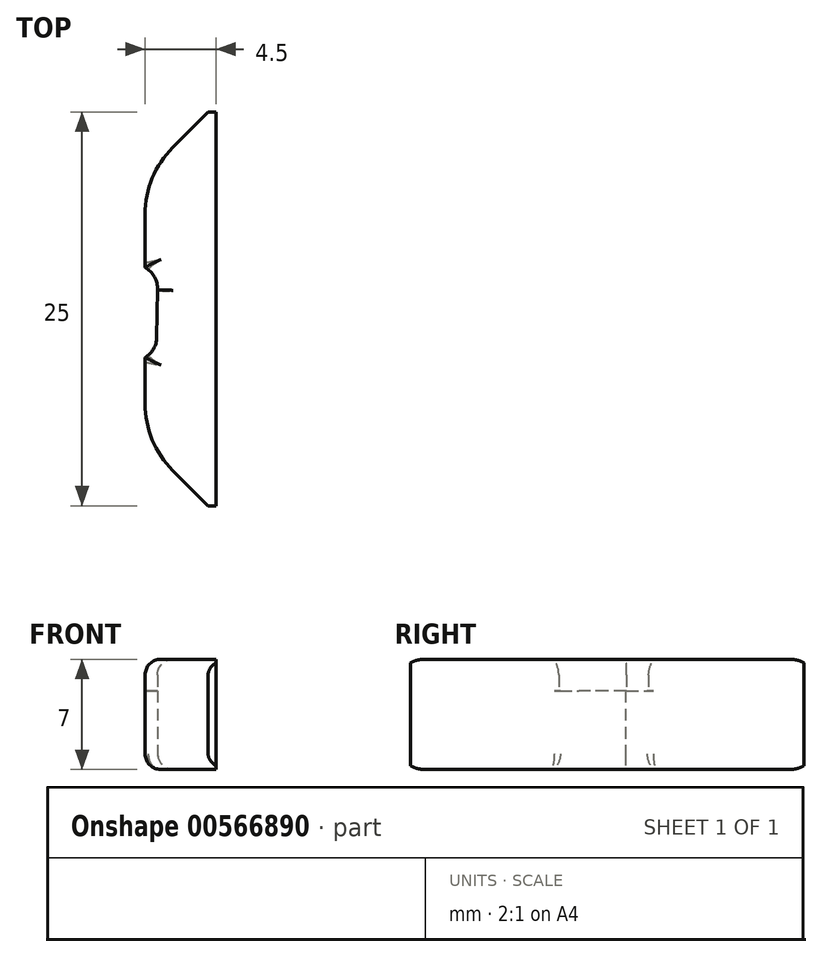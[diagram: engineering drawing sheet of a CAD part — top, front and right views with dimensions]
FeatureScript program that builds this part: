
annotation { "Feature Type Name" : "Feature", "Feature Type Description" : "" }
export const myFeature = defineFeature(function(context is Context, id is Id, definition is map)
    precondition{}
    {
        {
            var Q0;
            Q0=qCreatedBy(makeId("Top.planeOp"),FACE);
            var sketch = newSketch(context, id + "F0", { "sketchPlane" : qUnion([Q0])});
            skLineSegment(sketch, "E0.bottom", {"start": v(2.25, -12.5) * mm, "end": v(-2.25, -12.5) * mm});
            skLineSegment(sketch, "E0.top", {"start": v(2.25, 12.5) * mm, "end": v(-2.25, 12.5) * mm});
            skLineSegment(sketch, "E0.left", {"start": v(2.25, -12.5) * mm, "end": v(2.25, 12.5) * mm});
            skLineSegment(sketch, "E0.right", {"start": v(-2.25, -12.5) * mm, "end": v(-2.25, 12.5) * mm});
            skPoint(sketch, "E0.middle", {"position": v(0, 0) * mm});
            skPoint(sketch, "E1", {"position": v(-2.25, 0) * mm});
            skCircle(sketch, "E2", {"center": v(-2.95, 1.33) * mm, "radius": 1.5 * mm});
            skPoint(sketch, "E2.second.point", {"position": v(-2.25, 2.65) * mm});
            skPoint(sketch, "E2.third.point", {"position": v(-3.94, 2.45) * mm});
            skCircle(sketch, "E3", {"center": v(-2.99, -1.8) * mm, "radius": 1.5 * mm});
            skLineSegment(sketch, "E4", {"start": v(-1.46, 1.46) * mm, "end": v(-1.49, -1.8) * mm});
            skSolve(sketch);
        }
        {
            var Q0;
            Q0=makeQuery(id+"F0.imprint","IMPRINT",FACE,{"disambiguationData":[TD([[makeQuery(id+"F0.imprint","IMPRINT",EDGE,{"derivedFrom":sQuery(id+"F0.wireOp",EDGE,"E0.bottom")}),-1.0]])]});
            var Q1;
            Q1 = qSketchRegion(id + "F2", true);
            extrude(context, id + "F1", {"entities" : qUnion([Q0, Q1]), "depth" : 2 * mm, "offsetDistance" : 25 * mm});
        }
        {
            var Q0;
            Q0=makeQuery(id+"F1.opExtrude","CAP_FACE",FACE,{"disambiguationData":[OSD([sQuery(id+"F0.wireOp",EDGE,"E0.bottom"),sQuery(id+"F0.wireOp",EDGE,"E0.top"),sQuery(id+"F0.wireOp",EDGE,"E0.left"),sQuery(id+"F0.wireOp",EDGE,"E0.right"),sQuery(id+"F0.wireOp",EDGE,"E2"),sQuery(id+"F0.wireOp",EDGE,"E3"),sQuery(id+"F0.wireOp",EDGE,"E4")])],"isStart":false});
            var sketch = newSketch(context, id + "F2", { "sketchPlane" : qUnion([Q0])});
            skLineSegment(sketch, "E5.bottom", {"start": v(-2.25, 12.5) * mm, "end": v(2.25, 12.5) * mm});
            skLineSegment(sketch, "E5.top", {"start": v(-2.25, -12.5) * mm, "end": v(2.25, -12.5) * mm});
            skLineSegment(sketch, "E5.left", {"start": v(-2.25, 12.5) * mm, "end": v(-2.25, 5.3) * mm});
            skLineSegment(sketch, "E5.right", {"start": v(2.25, 12.5) * mm, "end": v(2.25, -12.5) * mm});
            skLineSegment(sketch, "E6.trimOffspring", {"start": v(-2.25, -3.1) * mm, "end": v(-2.25, -4.4) * mm});
            skArc(sketch, "E7", {"start": v(-1.46, 1.15) * mm, "mid": v(-1.62, 2.02) * mm, "end": v(-2.25, 2.65) * mm});
            skLineSegment(sketch, "E8", {"start": v(-1.46, 1.46) * mm, "end": v(-1.46, 1.15) * mm});
            skLineSegment(sketch, "E9", {"start": v(-1.48, -0.94) * mm, "end": v(-1.49, -1.8) * mm});
            skLineSegment(sketch, "E10", {"start": v(-1.49, -1.8) * mm, "end": v(-1.52, -2.12) * mm});
            skArc(sketch, "E11.0", {"start": v(0.03, 0.97) * mm, "mid": v(-0.3, 2.72) * mm, "end": v(-1.55, 3.98) * mm});
            skLineSegment(sketch, "E12.0", {"start": v(0.04, 1.16) * mm, "end": v(0.01, -1.8) * mm});
            skArc(sketch, "E13.0", {"start": v(-1.51, -4.4) * mm, "mid": v(-0.4, -3.3) * mm, "end": v(0.01, -1.8) * mm});
            skLineSegment(sketch, "E14", {"start": v(-1.55, 3.98) * mm, "end": v(-2.25, 3.98) * mm});
            skLineSegment(sketch, "E15", {"start": v(-1.51, -4.4) * mm, "end": v(-2.25, -4.4) * mm});
            skArc(sketch, "E16.0", {"start": v(1.52, 0.8) * mm, "mid": v(1.03, 3.42) * mm, "end": v(-0.85, 5.3) * mm});
            skLineSegment(sketch, "E17.0", {"start": v(1.54, 1.14) * mm, "end": v(1.51, -1.82) * mm});
            skArc(sketch, "E18.0", {"start": v(-0.78, -5.72) * mm, "mid": v(0.9, -4.07) * mm, "end": v(1.51, -1.8) * mm});
            skLineSegment(sketch, "E19", {"start": v(-0.85, 5.3) * mm, "end": v(-2.25, 5.3) * mm});
            skLineSegment(sketch, "E20", {"start": v(-0.78, -5.72) * mm, "end": v(-2.25, -5.72) * mm});
            skLineSegment(sketch, "E21.trimOffspring", {"start": v(-2.25, 3.98) * mm, "end": v(-2.25, 2.65) * mm});
            skLineSegment(sketch, "E22.trimOffspring", {"start": v(-2.25, -5.72) * mm, "end": v(-2.25, -12.5) * mm});
            skSolve(sketch);
        }
        {
            var Q0;
            {var subQ14=sQuery(id+"F2.wireOp",EDGE,"E6.trimOffspring");Q0=makeQuery(id+"F2.imprint","IMPRINT",FACE,{"disambiguationData":[TD([[makeQuery(id+"F2.imprint","IMPRINT",EDGE,{"derivedFrom":subQ14}),-1.0]])]});}
            var Q1;
            Q1=makeQuery(id+"F2.imprint","IMPRINT",FACE,{"disambiguationData":[TD([[makeQuery(id+"F2.imprint","IMPRINT",EDGE,{"derivedFrom":sQuery(id+"F2.wireOp",EDGE,"E5.bottom")}),1.0]])]});
            extrude(context, id + "F3", {"entities" : qUnion([Q0, Q1]), "operationType" : NewBodyOperationType.ADD, "depth" : 3 * mm, "offsetDistance" : 25 * mm});
        }
        {
            var Q0;
            Q0=makeQuery(id+"F3.opExtrude","CAP_FACE",FACE,{"disambiguationData":[OSD([sQuery(id+"F2.wireOp",EDGE,"E5.bottom"),sQuery(id+"F2.wireOp",EDGE,"E5.top"),sQuery(id+"F2.wireOp",EDGE,"E5.left"),sQuery(id+"F2.wireOp",EDGE,"E5.right"),sQuery(id+"F2.wireOp",EDGE,"E16.0"),sQuery(id+"F2.wireOp",EDGE,"E17.0"),sQuery(id+"F2.wireOp",EDGE,"E18.0"),sQuery(id+"F2.wireOp",EDGE,"E19"),sQuery(id+"F2.wireOp",EDGE,"E20"),sQuery(id+"F2.wireOp",EDGE,"E22.trimOffspring")])],"isStart":false});
            var sketch = newSketch(context, id + "F4", { "sketchPlane" : qUnion([Q0])});
            skLineSegment(sketch, "E23.bottom", {"start": v(-2.25, 12.5) * mm, "end": v(2.25, 12.5) * mm});
            skLineSegment(sketch, "E23.top", {"start": v(-2.25, -12.5) * mm, "end": v(2.25, -12.5) * mm});
            skLineSegment(sketch, "E23.left", {"start": v(-2.25, 12.5) * mm, "end": v(-2.25, 2.63) * mm});
            skLineSegment(sketch, "E23.right", {"start": v(2.25, 12.5) * mm, "end": v(2.25, -12.5) * mm});
            skArc(sketch, "E24", {"start": v(-1.47, 1.22) * mm, "mid": v(-1.65, 2.04) * mm, "end": v(-2.25, 2.63) * mm});
            skArc(sketch, "E25", {"start": v(-2.25, -3.08) * mm, "mid": v(-1.71, -2.54) * mm, "end": v(-1.5, -1.81) * mm});
            skLineSegment(sketch, "E26", {"start": v(-1.47, 1.22) * mm, "end": v(-1.5, -1.81) * mm});
            skLineSegment(sketch, "E27.trimOffspring", {"start": v(-2.25, -3.08) * mm, "end": v(-2.25, -12.5) * mm});
            skSolve(sketch);
        }
        {
            var Q0;
            Q0 = qSketchRegion(id + "F4", true);
            extrude(context, id + "F5", {"entities" : qUnion([Q0]), "operationType" : NewBodyOperationType.ADD, "depth" : 2 * mm, "offsetDistance" : 25 * mm});
        }
        {
            var Q0;
            Q0=makeQuery(id+"F3.opExtrude","SWEPT_EDGE",EDGE,{"disambiguationData":[OSD([sQuery(id+"F0.wireOp",EDGE,"E0.right"),sQuery(id+"F2.wireOp",EDGE,"E6.trimOffspring"),sQuery(id+"F2.wireOp",EDGE,"E15")])]});
            var Q1;
            Q1=makeQuery(id+"F3.opExtrude","SWEPT_EDGE",EDGE,{"disambiguationData":[OSD([sQuery(id+"F0.wireOp",EDGE,"E0.right"),sQuery(id+"F2.wireOp",EDGE,"E14"),sQuery(id+"F2.wireOp",EDGE,"E21.trimOffspring")])]});
            fillet(context, id + "F6", {"entities" : qUnion([Q0, Q1]), "radius" : .5 * mm, "tangentPropagation" : true, "allowEdgeOverflow" : false});
        }
        {
            var Q0;
            Q0=makeQuery(id+"F5.boolean.opBoolean","MERGE",EDGE,{"derivedFrom":[makeQuery(id+"F3.boolean.opBoolean","MERGE",EDGE,{"derivedFrom":[makeQuery(id+"F1.opExtrude","SWEPT_EDGE",EDGE,{"disambiguationData":[OSD([sQuery(id+"F0.wireOp",EDGE,"E0.top"),sQuery(id+"F0.wireOp",EDGE,"E0.right")])]}),makeQuery(id+"F3.opExtrude","SWEPT_EDGE",EDGE,{"disambiguationData":[OSD([sQuery(id+"F2.wireOp",EDGE,"E5.bottom"),sQuery(id+"F2.wireOp",EDGE,"E5.left")])]})]}),makeQuery(id+"F5.opExtrude","SWEPT_EDGE",EDGE,{"disambiguationData":[OSD([sQuery(id+"F4.wireOp",EDGE,"E23.bottom"),sQuery(id+"F4.wireOp",EDGE,"E23.left")])]})]});
            var Q1;
            Q1=makeQuery(id+"F5.boolean.opBoolean","MERGE",EDGE,{"derivedFrom":[makeQuery(id+"F3.boolean.opBoolean","MERGE",EDGE,{"derivedFrom":[makeQuery(id+"F1.opExtrude","SWEPT_EDGE",EDGE,{"disambiguationData":[OSD([sQuery(id+"F0.wireOp",EDGE,"E0.bottom"),sQuery(id+"F0.wireOp",EDGE,"E0.right")])]}),makeQuery(id+"F3.opExtrude","SWEPT_EDGE",EDGE,{"disambiguationData":[OSD([sQuery(id+"F2.wireOp",EDGE,"E5.top"),sQuery(id+"F2.wireOp",EDGE,"E22.trimOffspring")])]})]}),makeQuery(id+"F5.opExtrude","SWEPT_EDGE",EDGE,{"disambiguationData":[OSD([sQuery(id+"F4.wireOp",EDGE,"E23.top"),sQuery(id+"F4.wireOp",EDGE,"E27.trimOffspring")])]})]});
            chamfer(context, id + "F7", {"entities" : qUnion([Q0, Q1]), "width" : 4 * mm, "tangentPropagation" : true});
        }
        {
            var Q0;
            {var subQ0=sQuery(id+"F4.wireOp",EDGE,"E23.left");var subQ1=sQuery(id+"F2.wireOp",EDGE,"E5.left");var subQ2=sQuery(id+"F0.wireOp",EDGE,"E0.right");var subQ3=sQuery(id+"F0.wireOp",EDGE,"E0.top");Q0=makeQuery(id+"F7.opChamfer","BLEND_EDGE",EDGE,{"blendedFrom":[makeQuery(id+"F5.boolean.opBoolean","MERGE",EDGE,{"derivedFrom":[makeQuery(id+"F3.boolean.opBoolean","MERGE",EDGE,{"derivedFrom":[makeQuery(id+"F1.opExtrude","SWEPT_EDGE",EDGE,{"disambiguationData":[OSD([subQ3,subQ2])]}),makeQuery(id+"F3.opExtrude","SWEPT_EDGE",EDGE,{"disambiguationData":[OSD([sQuery(id+"F2.wireOp",EDGE,"E5.bottom"),subQ1])]})]}),makeQuery(id+"F5.opExtrude","SWEPT_EDGE",EDGE,{"disambiguationData":[OSD([sQuery(id+"F4.wireOp",EDGE,"E23.bottom"),subQ0])]})]}),makeQuery(id+"F5.boolean.opBoolean","MERGE",FACE,{"derivedFrom":[makeQuery(id+"F3.boolean.opBoolean","MERGE",FACE,{"derivedFrom":[makeQuery(id+"F1.opExtrude","SWEPT_FACE",FACE,{"disambiguationData":[OSD([subQ2]),TDD([makeQuery(id+"F0.imprint","IMPRINT",EDGE,{"disambiguationData":[TD([[makeQuery(id+"F0.imprint","INTERSECT",VERTEX,{"derivedFrom":[subQ3,subQ2]}),1.0]])],"derivedFrom":subQ2})])]}),makeQuery(id+"F3.opExtrude","SWEPT_FACE",FACE,{"disambiguationData":[OSD([subQ1])]}),makeQuery(id+"F3.opExtrude","SWEPT_FACE",FACE,{"disambiguationData":[OSD([sQuery(id+"F2.wireOp",EDGE,"E21.trimOffspring")])]})]}),makeQuery(id+"F5.opExtrude","SWEPT_FACE",FACE,{"disambiguationData":[OSD([subQ0])]})]})],"blendedInto":[makeQuery(id+"F5.boolean.opBoolean","MERGE",FACE,{"derivedFrom":[makeQuery(id+"F3.boolean.opBoolean","MERGE",FACE,{"derivedFrom":[makeQuery(id+"F1.opExtrude","SWEPT_FACE",FACE,{"disambiguationData":[OSD([subQ2]),TDD([makeQuery(id+"F0.imprint","IMPRINT",EDGE,{"disambiguationData":[TD([[makeQuery(id+"F0.imprint","INTERSECT",VERTEX,{"derivedFrom":[subQ3,subQ2]}),1.0]])],"derivedFrom":subQ2})])]}),makeQuery(id+"F3.opExtrude","SWEPT_FACE",FACE,{"disambiguationData":[OSD([subQ1])]}),makeQuery(id+"F3.opExtrude","SWEPT_FACE",FACE,{"disambiguationData":[OSD([sQuery(id+"F2.wireOp",EDGE,"E21.trimOffspring")])]})]}),makeQuery(id+"F5.opExtrude","SWEPT_FACE",FACE,{"disambiguationData":[OSD([subQ0])]})]})]});}
            var Q1;
            {var subQ0=sQuery(id+"F4.wireOp",EDGE,"E27.trimOffspring");var subQ1=sQuery(id+"F2.wireOp",EDGE,"E22.trimOffspring");var subQ2=sQuery(id+"F0.wireOp",EDGE,"E0.right");var subQ3=sQuery(id+"F0.wireOp",EDGE,"E0.bottom");Q1=makeQuery(id+"F7.opChamfer","BLEND_EDGE",EDGE,{"blendedFrom":[makeQuery(id+"F5.boolean.opBoolean","MERGE",EDGE,{"derivedFrom":[makeQuery(id+"F3.boolean.opBoolean","MERGE",EDGE,{"derivedFrom":[makeQuery(id+"F1.opExtrude","SWEPT_EDGE",EDGE,{"disambiguationData":[OSD([subQ3,subQ2])]}),makeQuery(id+"F3.opExtrude","SWEPT_EDGE",EDGE,{"disambiguationData":[OSD([sQuery(id+"F2.wireOp",EDGE,"E5.top"),subQ1])]})]}),makeQuery(id+"F5.opExtrude","SWEPT_EDGE",EDGE,{"disambiguationData":[OSD([sQuery(id+"F4.wireOp",EDGE,"E23.top"),subQ0])]})]}),makeQuery(id+"F5.boolean.opBoolean","MERGE",FACE,{"derivedFrom":[makeQuery(id+"F3.boolean.opBoolean","MERGE",FACE,{"derivedFrom":[makeQuery(id+"F1.opExtrude","SWEPT_FACE",FACE,{"disambiguationData":[OSD([subQ2]),TDD([makeQuery(id+"F0.imprint","IMPRINT",EDGE,{"disambiguationData":[TD([[makeQuery(id+"F0.imprint","INTERSECT",VERTEX,{"derivedFrom":[subQ3,subQ2]}),-1.0]])],"derivedFrom":subQ2})])]}),makeQuery(id+"F3.opExtrude","SWEPT_FACE",FACE,{"disambiguationData":[OSD([sQuery(id+"F2.wireOp",EDGE,"E6.trimOffspring")])]}),makeQuery(id+"F3.opExtrude","SWEPT_FACE",FACE,{"disambiguationData":[OSD([subQ1])]})]}),makeQuery(id+"F5.opExtrude","SWEPT_FACE",FACE,{"disambiguationData":[OSD([subQ0])]})]})],"blendedInto":[makeQuery(id+"F5.boolean.opBoolean","MERGE",FACE,{"derivedFrom":[makeQuery(id+"F3.boolean.opBoolean","MERGE",FACE,{"derivedFrom":[makeQuery(id+"F1.opExtrude","SWEPT_FACE",FACE,{"disambiguationData":[OSD([subQ2]),TDD([makeQuery(id+"F0.imprint","IMPRINT",EDGE,{"disambiguationData":[TD([[makeQuery(id+"F0.imprint","INTERSECT",VERTEX,{"derivedFrom":[subQ3,subQ2]}),-1.0]])],"derivedFrom":subQ2})])]}),makeQuery(id+"F3.opExtrude","SWEPT_FACE",FACE,{"disambiguationData":[OSD([sQuery(id+"F2.wireOp",EDGE,"E6.trimOffspring")])]}),makeQuery(id+"F3.opExtrude","SWEPT_FACE",FACE,{"disambiguationData":[OSD([subQ1])]})]}),makeQuery(id+"F5.opExtrude","SWEPT_FACE",FACE,{"disambiguationData":[OSD([subQ0])]})]})]});}
            fillet(context, id + "F8", {"entities" : qUnion([Q0, Q1]), "radius" : 6 * mm, "tangentPropagation" : true, "allowEdgeOverflow" : false});
        }
        {
            var Q0;
            {var subQ0=sQuery(id+"F4.wireOp",EDGE,"E23.left");var subQ1=sQuery(id+"F4.wireOp",EDGE,"E23.bottom");Q0=makeQuery(id+"F7.opChamfer","BLEND_EDGE",EDGE,{"blendedFrom":[makeQuery(id+"F5.boolean.opBoolean","MERGE",EDGE,{"derivedFrom":[makeQuery(id+"F3.boolean.opBoolean","MERGE",EDGE,{"derivedFrom":[makeQuery(id+"F1.opExtrude","SWEPT_EDGE",EDGE,{"disambiguationData":[OSD([sQuery(id+"F0.wireOp",EDGE,"E0.top"),sQuery(id+"F0.wireOp",EDGE,"E0.right")])]}),makeQuery(id+"F3.opExtrude","SWEPT_EDGE",EDGE,{"disambiguationData":[OSD([sQuery(id+"F2.wireOp",EDGE,"E5.bottom"),sQuery(id+"F2.wireOp",EDGE,"E5.left")])]})]}),makeQuery(id+"F5.opExtrude","SWEPT_EDGE",EDGE,{"disambiguationData":[OSD([subQ1,subQ0])]})]}),makeQuery(id+"F5.opExtrude","CAP_FACE",FACE,{"disambiguationData":[OSD([subQ1,sQuery(id+"F4.wireOp",EDGE,"E23.top"),subQ0,sQuery(id+"F4.wireOp",EDGE,"E23.right"),sQuery(id+"F4.wireOp",EDGE,"E24"),sQuery(id+"F4.wireOp",EDGE,"E25"),sQuery(id+"F4.wireOp",EDGE,"E26"),sQuery(id+"F4.wireOp",EDGE,"E27.trimOffspring")])],"isStart":false})],"blendedInto":[makeQuery(id+"F5.opExtrude","CAP_FACE",FACE,{"disambiguationData":[OSD([subQ1,sQuery(id+"F4.wireOp",EDGE,"E23.top"),subQ0,sQuery(id+"F4.wireOp",EDGE,"E23.right"),sQuery(id+"F4.wireOp",EDGE,"E24"),sQuery(id+"F4.wireOp",EDGE,"E25"),sQuery(id+"F4.wireOp",EDGE,"E26"),sQuery(id+"F4.wireOp",EDGE,"E27.trimOffspring")])],"isStart":false})]});}
            var Q1;
            Q1=makeQuery(id+"F5.opExtrude","CAP_EDGE",EDGE,{"disambiguationData":[OSD([sQuery(id+"F4.wireOp",EDGE,"E24")])],"isStart":false});
            var Q2;
            Q2=makeQuery(id+"F5.opExtrude","CAP_EDGE",EDGE,{"disambiguationData":[OSD([sQuery(id+"F4.wireOp",EDGE,"E26")])],"isStart":false});
            var Q3;
            Q3=makeQuery(id+"F5.opExtrude","CAP_EDGE",EDGE,{"disambiguationData":[OSD([sQuery(id+"F4.wireOp",EDGE,"E25")])],"isStart":false});
            var Q4;
            {var subQ0=sQuery(id+"F4.wireOp",EDGE,"E27.trimOffspring");var subQ1=sQuery(id+"F4.wireOp",EDGE,"E23.top");var subQ2=sQuery(id+"F2.wireOp",EDGE,"E22.trimOffspring");var subQ3=sQuery(id+"F0.wireOp",EDGE,"E0.right");var subQ4=sQuery(id+"F0.wireOp",EDGE,"E0.bottom");Q4=makeQuery(id+"F8.opFillet","BLEND_EDGE",EDGE,{"blendedFrom":[makeQuery(id+"F7.opChamfer","BLEND_EDGE",EDGE,{"blendedFrom":[makeQuery(id+"F5.boolean.opBoolean","MERGE",EDGE,{"derivedFrom":[makeQuery(id+"F3.boolean.opBoolean","MERGE",EDGE,{"derivedFrom":[makeQuery(id+"F1.opExtrude","SWEPT_EDGE",EDGE,{"disambiguationData":[OSD([subQ4,subQ3])]}),makeQuery(id+"F3.opExtrude","SWEPT_EDGE",EDGE,{"disambiguationData":[OSD([sQuery(id+"F2.wireOp",EDGE,"E5.top"),subQ2])]})]}),makeQuery(id+"F5.opExtrude","SWEPT_EDGE",EDGE,{"disambiguationData":[OSD([subQ1,subQ0])]})]}),makeQuery(id+"F5.boolean.opBoolean","MERGE",FACE,{"derivedFrom":[makeQuery(id+"F3.boolean.opBoolean","MERGE",FACE,{"derivedFrom":[makeQuery(id+"F1.opExtrude","SWEPT_FACE",FACE,{"disambiguationData":[OSD([subQ3]),TDD([makeQuery(id+"F0.imprint","IMPRINT",EDGE,{"disambiguationData":[TD([[makeQuery(id+"F0.imprint","INTERSECT",VERTEX,{"derivedFrom":[subQ4,subQ3]}),-1.0]])],"derivedFrom":subQ3})])]}),makeQuery(id+"F3.opExtrude","SWEPT_FACE",FACE,{"disambiguationData":[OSD([sQuery(id+"F2.wireOp",EDGE,"E6.trimOffspring")])]}),makeQuery(id+"F3.opExtrude","SWEPT_FACE",FACE,{"disambiguationData":[OSD([subQ2])]})]}),makeQuery(id+"F5.opExtrude","SWEPT_FACE",FACE,{"disambiguationData":[OSD([subQ0])]})]})],"blendedInto":[makeQuery(id+"F5.boolean.opBoolean","MERGE",FACE,{"derivedFrom":[makeQuery(id+"F3.boolean.opBoolean","MERGE",FACE,{"derivedFrom":[makeQuery(id+"F1.opExtrude","SWEPT_FACE",FACE,{"disambiguationData":[OSD([subQ3]),TDD([makeQuery(id+"F0.imprint","IMPRINT",EDGE,{"disambiguationData":[TD([[makeQuery(id+"F0.imprint","INTERSECT",VERTEX,{"derivedFrom":[subQ4,subQ3]}),-1.0]])],"derivedFrom":subQ3})])]}),makeQuery(id+"F3.opExtrude","SWEPT_FACE",FACE,{"disambiguationData":[OSD([sQuery(id+"F2.wireOp",EDGE,"E6.trimOffspring")])]}),makeQuery(id+"F3.opExtrude","SWEPT_FACE",FACE,{"disambiguationData":[OSD([subQ2])]})]}),makeQuery(id+"F5.opExtrude","SWEPT_FACE",FACE,{"disambiguationData":[OSD([subQ0])]})]})]}),makeQuery(id+"F5.opExtrude","CAP_FACE",FACE,{"disambiguationData":[OSD([sQuery(id+"F4.wireOp",EDGE,"E23.bottom"),subQ1,sQuery(id+"F4.wireOp",EDGE,"E23.left"),sQuery(id+"F4.wireOp",EDGE,"E23.right"),sQuery(id+"F4.wireOp",EDGE,"E24"),sQuery(id+"F4.wireOp",EDGE,"E25"),sQuery(id+"F4.wireOp",EDGE,"E26"),subQ0])],"isStart":false})],"blendedInto":[makeQuery(id+"F5.opExtrude","CAP_FACE",FACE,{"disambiguationData":[OSD([sQuery(id+"F4.wireOp",EDGE,"E23.bottom"),subQ1,sQuery(id+"F4.wireOp",EDGE,"E23.left"),sQuery(id+"F4.wireOp",EDGE,"E23.right"),sQuery(id+"F4.wireOp",EDGE,"E24"),sQuery(id+"F4.wireOp",EDGE,"E25"),sQuery(id+"F4.wireOp",EDGE,"E26"),subQ0])],"isStart":false})]});}
            var Q5;
            {var subQ0=sQuery(id+"F4.wireOp",EDGE,"E27.trimOffspring");var subQ1=sQuery(id+"F4.wireOp",EDGE,"E23.top");Q5=makeQuery(id+"F7.opChamfer","BLEND_EDGE",EDGE,{"blendedFrom":[makeQuery(id+"F5.boolean.opBoolean","MERGE",EDGE,{"derivedFrom":[makeQuery(id+"F3.boolean.opBoolean","MERGE",EDGE,{"derivedFrom":[makeQuery(id+"F1.opExtrude","SWEPT_EDGE",EDGE,{"disambiguationData":[OSD([sQuery(id+"F0.wireOp",EDGE,"E0.bottom"),sQuery(id+"F0.wireOp",EDGE,"E0.right")])]}),makeQuery(id+"F3.opExtrude","SWEPT_EDGE",EDGE,{"disambiguationData":[OSD([sQuery(id+"F2.wireOp",EDGE,"E5.top"),sQuery(id+"F2.wireOp",EDGE,"E22.trimOffspring")])]})]}),makeQuery(id+"F5.opExtrude","SWEPT_EDGE",EDGE,{"disambiguationData":[OSD([subQ1,subQ0])]})]}),makeQuery(id+"F5.opExtrude","CAP_FACE",FACE,{"disambiguationData":[OSD([sQuery(id+"F4.wireOp",EDGE,"E23.bottom"),subQ1,sQuery(id+"F4.wireOp",EDGE,"E23.left"),sQuery(id+"F4.wireOp",EDGE,"E23.right"),sQuery(id+"F4.wireOp",EDGE,"E24"),sQuery(id+"F4.wireOp",EDGE,"E25"),sQuery(id+"F4.wireOp",EDGE,"E26"),subQ0])],"isStart":false})],"blendedInto":[makeQuery(id+"F5.opExtrude","CAP_FACE",FACE,{"disambiguationData":[OSD([sQuery(id+"F4.wireOp",EDGE,"E23.bottom"),subQ1,sQuery(id+"F4.wireOp",EDGE,"E23.left"),sQuery(id+"F4.wireOp",EDGE,"E23.right"),sQuery(id+"F4.wireOp",EDGE,"E24"),sQuery(id+"F4.wireOp",EDGE,"E25"),sQuery(id+"F4.wireOp",EDGE,"E26"),subQ0])],"isStart":false})]});}
            var Q6;
            {var subQ0=sQuery(id+"F0.wireOp",EDGE,"E0.right");var subQ1=sQuery(id+"F0.wireOp",EDGE,"E0.bottom");Q6=makeQuery(id+"F7.opChamfer","BLEND_EDGE",EDGE,{"blendedFrom":[makeQuery(id+"F5.boolean.opBoolean","MERGE",EDGE,{"derivedFrom":[makeQuery(id+"F3.boolean.opBoolean","MERGE",EDGE,{"derivedFrom":[makeQuery(id+"F1.opExtrude","SWEPT_EDGE",EDGE,{"disambiguationData":[OSD([subQ1,subQ0])]}),makeQuery(id+"F3.opExtrude","SWEPT_EDGE",EDGE,{"disambiguationData":[OSD([sQuery(id+"F2.wireOp",EDGE,"E5.top"),sQuery(id+"F2.wireOp",EDGE,"E22.trimOffspring")])]})]}),makeQuery(id+"F5.opExtrude","SWEPT_EDGE",EDGE,{"disambiguationData":[OSD([sQuery(id+"F4.wireOp",EDGE,"E23.top"),sQuery(id+"F4.wireOp",EDGE,"E27.trimOffspring")])]})]}),makeQuery(id+"F1.opExtrude","CAP_FACE",FACE,{"disambiguationData":[OSD([subQ1,sQuery(id+"F0.wireOp",EDGE,"E0.top"),sQuery(id+"F0.wireOp",EDGE,"E0.left"),subQ0,sQuery(id+"F0.wireOp",EDGE,"E2"),sQuery(id+"F0.wireOp",EDGE,"E3"),sQuery(id+"F0.wireOp",EDGE,"E4")])],"isStart":true})],"blendedInto":[makeQuery(id+"F1.opExtrude","CAP_FACE",FACE,{"disambiguationData":[OSD([subQ1,sQuery(id+"F0.wireOp",EDGE,"E0.top"),sQuery(id+"F0.wireOp",EDGE,"E0.left"),subQ0,sQuery(id+"F0.wireOp",EDGE,"E2"),sQuery(id+"F0.wireOp",EDGE,"E3"),sQuery(id+"F0.wireOp",EDGE,"E4")])],"isStart":true})]});}
            var Q7;
            {var subQ0=sQuery(id+"F0.wireOp",EDGE,"E3");var subQ1=sQuery(id+"F0.wireOp",EDGE,"E0.right");var subQ2=sQuery(id+"F0.wireOp",EDGE,"E0.bottom");var subQ3=sQuery(id+"F4.wireOp",EDGE,"E27.trimOffspring");var subQ4=sQuery(id+"F2.wireOp",EDGE,"E22.trimOffspring");Q7=makeQuery(id+"F8.opFillet","BLEND_EDGE",EDGE,{"blendedFrom":[makeQuery(id+"F7.opChamfer","BLEND_EDGE",EDGE,{"blendedFrom":[makeQuery(id+"F5.boolean.opBoolean","MERGE",EDGE,{"derivedFrom":[makeQuery(id+"F3.boolean.opBoolean","MERGE",EDGE,{"derivedFrom":[makeQuery(id+"F1.opExtrude","SWEPT_EDGE",EDGE,{"disambiguationData":[OSD([subQ2,subQ1])]}),makeQuery(id+"F3.opExtrude","SWEPT_EDGE",EDGE,{"disambiguationData":[OSD([sQuery(id+"F2.wireOp",EDGE,"E5.top"),subQ4])]})]}),makeQuery(id+"F5.opExtrude","SWEPT_EDGE",EDGE,{"disambiguationData":[OSD([sQuery(id+"F4.wireOp",EDGE,"E23.top"),subQ3])]})]}),makeQuery(id+"F5.boolean.opBoolean","MERGE",FACE,{"derivedFrom":[makeQuery(id+"F3.boolean.opBoolean","MERGE",FACE,{"derivedFrom":[makeQuery(id+"F1.opExtrude","SWEPT_FACE",FACE,{"disambiguationData":[OSD([subQ1]),TDD([makeQuery(id+"F0.imprint","IMPRINT",EDGE,{"disambiguationData":[TD([[makeQuery(id+"F0.imprint","INTERSECT",VERTEX,{"derivedFrom":[subQ2,subQ1]}),-1.0]])],"derivedFrom":subQ1})])]}),makeQuery(id+"F3.opExtrude","SWEPT_FACE",FACE,{"disambiguationData":[OSD([sQuery(id+"F2.wireOp",EDGE,"E6.trimOffspring")])]}),makeQuery(id+"F3.opExtrude","SWEPT_FACE",FACE,{"disambiguationData":[OSD([subQ4])]})]}),makeQuery(id+"F5.opExtrude","SWEPT_FACE",FACE,{"disambiguationData":[OSD([subQ3])]})]})],"blendedInto":[makeQuery(id+"F5.boolean.opBoolean","MERGE",FACE,{"derivedFrom":[makeQuery(id+"F3.boolean.opBoolean","MERGE",FACE,{"derivedFrom":[makeQuery(id+"F1.opExtrude","SWEPT_FACE",FACE,{"disambiguationData":[OSD([subQ1]),TDD([makeQuery(id+"F0.imprint","IMPRINT",EDGE,{"disambiguationData":[TD([[makeQuery(id+"F0.imprint","INTERSECT",VERTEX,{"derivedFrom":[subQ2,subQ1]}),-1.0]])],"derivedFrom":subQ1})])]}),makeQuery(id+"F3.opExtrude","SWEPT_FACE",FACE,{"disambiguationData":[OSD([sQuery(id+"F2.wireOp",EDGE,"E6.trimOffspring")])]}),makeQuery(id+"F3.opExtrude","SWEPT_FACE",FACE,{"disambiguationData":[OSD([subQ4])]})]}),makeQuery(id+"F5.opExtrude","SWEPT_FACE",FACE,{"disambiguationData":[OSD([subQ3])]})]})]}),makeQuery(id+"F1.opExtrude","CAP_FACE",FACE,{"disambiguationData":[OSD([subQ2,sQuery(id+"F0.wireOp",EDGE,"E0.top"),sQuery(id+"F0.wireOp",EDGE,"E0.left"),subQ1,sQuery(id+"F0.wireOp",EDGE,"E2"),subQ0,sQuery(id+"F0.wireOp",EDGE,"E4")])],"isStart":true})],"blendedInto":[makeQuery(id+"F1.opExtrude","CAP_FACE",FACE,{"disambiguationData":[OSD([subQ2,sQuery(id+"F0.wireOp",EDGE,"E0.top"),sQuery(id+"F0.wireOp",EDGE,"E0.left"),subQ1,sQuery(id+"F0.wireOp",EDGE,"E2"),subQ0,sQuery(id+"F0.wireOp",EDGE,"E4")])],"isStart":true})]});}
            var Q8;
            {var subQ0=sQuery(id+"F0.wireOp",EDGE,"E0.right");Q8=makeQuery(id+"F1.opExtrude","CAP_EDGE",EDGE,{"disambiguationData":[OSD([subQ0]),TDD([makeQuery(id+"F0.imprint","IMPRINT",EDGE,{"disambiguationData":[TD([[makeQuery(id+"F0.imprint","INTERSECT",VERTEX,{"derivedFrom":[sQuery(id+"F0.wireOp",EDGE,"E0.bottom"),subQ0]}),-1.0]])],"derivedFrom":subQ0})])],"isStart":true});}
            var Q9;
            Q9=makeQuery(id+"F1.opExtrude","CAP_EDGE",EDGE,{"disambiguationData":[OSD([sQuery(id+"F0.wireOp",EDGE,"E3")])],"isStart":true});
            var Q10;
            Q10=makeQuery(id+"F1.opExtrude","CAP_EDGE",EDGE,{"disambiguationData":[OSD([sQuery(id+"F0.wireOp",EDGE,"E4")])],"isStart":true});
            var Q11;
            Q11=makeQuery(id+"F1.opExtrude","CAP_EDGE",EDGE,{"disambiguationData":[OSD([sQuery(id+"F0.wireOp",EDGE,"E2")])],"isStart":true});
            var Q12;
            {var subQ0=sQuery(id+"F0.wireOp",EDGE,"E0.right");Q12=makeQuery(id+"F1.opExtrude","CAP_EDGE",EDGE,{"disambiguationData":[OSD([subQ0]),TDD([makeQuery(id+"F0.imprint","IMPRINT",EDGE,{"disambiguationData":[TD([[makeQuery(id+"F0.imprint","INTERSECT",VERTEX,{"derivedFrom":[sQuery(id+"F0.wireOp",EDGE,"E0.top"),subQ0]}),1.0]])],"derivedFrom":subQ0})])],"isStart":true});}
            var Q13;
            {var subQ0=sQuery(id+"F0.wireOp",EDGE,"E2");var subQ1=sQuery(id+"F0.wireOp",EDGE,"E0.right");var subQ2=sQuery(id+"F0.wireOp",EDGE,"E0.top");var subQ3=sQuery(id+"F4.wireOp",EDGE,"E23.left");var subQ4=sQuery(id+"F2.wireOp",EDGE,"E5.left");Q13=makeQuery(id+"F8.opFillet","BLEND_EDGE",EDGE,{"blendedFrom":[makeQuery(id+"F7.opChamfer","BLEND_EDGE",EDGE,{"blendedFrom":[makeQuery(id+"F5.boolean.opBoolean","MERGE",EDGE,{"derivedFrom":[makeQuery(id+"F3.boolean.opBoolean","MERGE",EDGE,{"derivedFrom":[makeQuery(id+"F1.opExtrude","SWEPT_EDGE",EDGE,{"disambiguationData":[OSD([subQ2,subQ1])]}),makeQuery(id+"F3.opExtrude","SWEPT_EDGE",EDGE,{"disambiguationData":[OSD([sQuery(id+"F2.wireOp",EDGE,"E5.bottom"),subQ4])]})]}),makeQuery(id+"F5.opExtrude","SWEPT_EDGE",EDGE,{"disambiguationData":[OSD([sQuery(id+"F4.wireOp",EDGE,"E23.bottom"),subQ3])]})]}),makeQuery(id+"F5.boolean.opBoolean","MERGE",FACE,{"derivedFrom":[makeQuery(id+"F3.boolean.opBoolean","MERGE",FACE,{"derivedFrom":[makeQuery(id+"F1.opExtrude","SWEPT_FACE",FACE,{"disambiguationData":[OSD([subQ1]),TDD([makeQuery(id+"F0.imprint","IMPRINT",EDGE,{"disambiguationData":[TD([[makeQuery(id+"F0.imprint","INTERSECT",VERTEX,{"derivedFrom":[subQ2,subQ1]}),1.0]])],"derivedFrom":subQ1})])]}),makeQuery(id+"F3.opExtrude","SWEPT_FACE",FACE,{"disambiguationData":[OSD([subQ4])]}),makeQuery(id+"F3.opExtrude","SWEPT_FACE",FACE,{"disambiguationData":[OSD([sQuery(id+"F2.wireOp",EDGE,"E21.trimOffspring")])]})]}),makeQuery(id+"F5.opExtrude","SWEPT_FACE",FACE,{"disambiguationData":[OSD([subQ3])]})]})],"blendedInto":[makeQuery(id+"F5.boolean.opBoolean","MERGE",FACE,{"derivedFrom":[makeQuery(id+"F3.boolean.opBoolean","MERGE",FACE,{"derivedFrom":[makeQuery(id+"F1.opExtrude","SWEPT_FACE",FACE,{"disambiguationData":[OSD([subQ1]),TDD([makeQuery(id+"F0.imprint","IMPRINT",EDGE,{"disambiguationData":[TD([[makeQuery(id+"F0.imprint","INTERSECT",VERTEX,{"derivedFrom":[subQ2,subQ1]}),1.0]])],"derivedFrom":subQ1})])]}),makeQuery(id+"F3.opExtrude","SWEPT_FACE",FACE,{"disambiguationData":[OSD([subQ4])]}),makeQuery(id+"F3.opExtrude","SWEPT_FACE",FACE,{"disambiguationData":[OSD([sQuery(id+"F2.wireOp",EDGE,"E21.trimOffspring")])]})]}),makeQuery(id+"F5.opExtrude","SWEPT_FACE",FACE,{"disambiguationData":[OSD([subQ3])]})]})]}),makeQuery(id+"F1.opExtrude","CAP_FACE",FACE,{"disambiguationData":[OSD([sQuery(id+"F0.wireOp",EDGE,"E0.bottom"),subQ2,sQuery(id+"F0.wireOp",EDGE,"E0.left"),subQ1,subQ0,sQuery(id+"F0.wireOp",EDGE,"E3"),sQuery(id+"F0.wireOp",EDGE,"E4")])],"isStart":true})],"blendedInto":[makeQuery(id+"F1.opExtrude","CAP_FACE",FACE,{"disambiguationData":[OSD([sQuery(id+"F0.wireOp",EDGE,"E0.bottom"),subQ2,sQuery(id+"F0.wireOp",EDGE,"E0.left"),subQ1,subQ0,sQuery(id+"F0.wireOp",EDGE,"E3"),sQuery(id+"F0.wireOp",EDGE,"E4")])],"isStart":true})]});}
            var Q14;
            {var subQ0=sQuery(id+"F0.wireOp",EDGE,"E0.right");var subQ1=sQuery(id+"F0.wireOp",EDGE,"E0.top");Q14=makeQuery(id+"F7.opChamfer","BLEND_EDGE",EDGE,{"blendedFrom":[makeQuery(id+"F5.boolean.opBoolean","MERGE",EDGE,{"derivedFrom":[makeQuery(id+"F3.boolean.opBoolean","MERGE",EDGE,{"derivedFrom":[makeQuery(id+"F1.opExtrude","SWEPT_EDGE",EDGE,{"disambiguationData":[OSD([subQ1,subQ0])]}),makeQuery(id+"F3.opExtrude","SWEPT_EDGE",EDGE,{"disambiguationData":[OSD([sQuery(id+"F2.wireOp",EDGE,"E5.bottom"),sQuery(id+"F2.wireOp",EDGE,"E5.left")])]})]}),makeQuery(id+"F5.opExtrude","SWEPT_EDGE",EDGE,{"disambiguationData":[OSD([sQuery(id+"F4.wireOp",EDGE,"E23.bottom"),sQuery(id+"F4.wireOp",EDGE,"E23.left")])]})]}),makeQuery(id+"F1.opExtrude","CAP_FACE",FACE,{"disambiguationData":[OSD([sQuery(id+"F0.wireOp",EDGE,"E0.bottom"),subQ1,sQuery(id+"F0.wireOp",EDGE,"E0.left"),subQ0,sQuery(id+"F0.wireOp",EDGE,"E2"),sQuery(id+"F0.wireOp",EDGE,"E3"),sQuery(id+"F0.wireOp",EDGE,"E4")])],"isStart":true})],"blendedInto":[makeQuery(id+"F1.opExtrude","CAP_FACE",FACE,{"disambiguationData":[OSD([sQuery(id+"F0.wireOp",EDGE,"E0.bottom"),subQ1,sQuery(id+"F0.wireOp",EDGE,"E0.left"),subQ0,sQuery(id+"F0.wireOp",EDGE,"E2"),sQuery(id+"F0.wireOp",EDGE,"E3"),sQuery(id+"F0.wireOp",EDGE,"E4")])],"isStart":true})]});}
            fillet(context, id + "F9", {"entities" : qUnion([Q0, Q1, Q2, Q3, Q4, Q5, Q6, Q7, Q8, Q9, Q10, Q11, Q12, Q13, Q14]), "radius" : 1 * mm, "tangentPropagation" : true, "allowEdgeOverflow" : false});
        }
    });
